FCSTD DOCUMENT  (FreeCAD 0.21R32532 (Git))
Label: m,
License: All rights reserved
LicenseURL: http://en.wikipedia.org/wiki/All_rights_reserved
objects: Sketcher::SketchObject×2, PartDesign::Body×1
note: 3 computed .brp shape members not serialized (recipe doc carries the construction recipe); baked Part::Feature solids carry a one-line shape summary decoded from their .brp

FEATURE [Sketcher::SketchObject] Sketch
  FullyConstrained = true
  MapMode = 5
  Support = -> [XY_Plane]
  sketch-geometry (9):
    g0: LineSegment StartX=6.55 StartY=0 StartZ=0 EndX=6.55 EndY=1.5 EndZ=0
    g1: LineSegment StartX=-7.8 StartY=1.5 StartZ=0 EndX=-7.8 EndY=28 EndZ=0
    g2: LineSegment StartX=-7.8 StartY=28 StartZ=0 EndX=-9.05 EndY=28 EndZ=0
    g3: LineSegment StartX=-9.05 StartY=28 StartZ=0 EndX=-9.05 EndY=42.75 EndZ=0
    g4: LineSegment StartX=-9.05 StartY=42.75 StartZ=0 EndX=31.45 EndY=42.75 EndZ=0
    g5: LineSegment StartX=31.45 StartY=42.75 StartZ=0 EndX=31.45 EndY=0 EndZ=0
    g6: LineSegment StartX=31.45 StartY=0 StartZ=0 EndX=6.55 EndY=0 EndZ=0
    g7: LineSegment StartX=6.55 StartY=1.5 StartZ=0 EndX=-6.55 EndY=1.5 EndZ=0
    g8: LineSegment StartX=-6.55 StartY=1.5 StartZ=0 EndX=-7.8 EndY=1.5 EndZ=0
  constraints (26):
    c: PointOnObject(g0,g-1)
    c: Vertical(g0)
    c: Coincident(g8,g1)
    c: Vertical(g1)
    c: Coincident(g1,g2)
    c: Horizontal(g2)
    c: Coincident(g2,g3)
    c: Vertical(g3)
    c: Coincident(g3,g4)
    c: Horizontal(g4)
    c: Coincident(g4,g5)
    c: PointOnObject(g5,g-1)
    c: Vertical(g5)
    c: Coincident(g5,g6)
    c: Coincident(g6,g0)
    c: DistanceX(g4,g4) = 40.5
    c: DistanceX(g2,g1) = 1.25
    c: Coincident(g7,g8)
    c: Symmetric(g7,g7,g-2)
    c: DistanceX(g7,g7) = 13.1
    c: DistanceX(g8,g8) = 1.25
    c: DistanceY(g5,g5) = 42.75
    c: DistanceY(g3,g3) = 14.75
    c: Horizontal(g8)
    c: DistanceY(g0,g7) = 1.5
    c: Coincident(g0,g7)
FEATURE [PartDesign::Body] Body
  Group = -> [Sketch]
  Origin = -> Origin
FEATURE [Sketcher::SketchObject] Sketch001
  FullyConstrained = false
  sketch-geometry (2):
    g0: Circle CenterX=10.8 CenterY=-4.25 CenterZ=0 NormalX=0 NormalY=0 NormalZ=1 AngleXU=0 Radius=1.7
    g1: Circle CenterX=0 CenterY=-149.644 CenterZ=0 NormalX=0 NormalY=0 NormalZ=1 AngleXU=0 Radius=13.1947
  constraints (4):
    c: PointOnObject(g1,g-2)
    c: DistanceY(g0) = -4.25
    c: DistanceX(g0) = 10.8
    c: Diameter(g0) = 3.4
